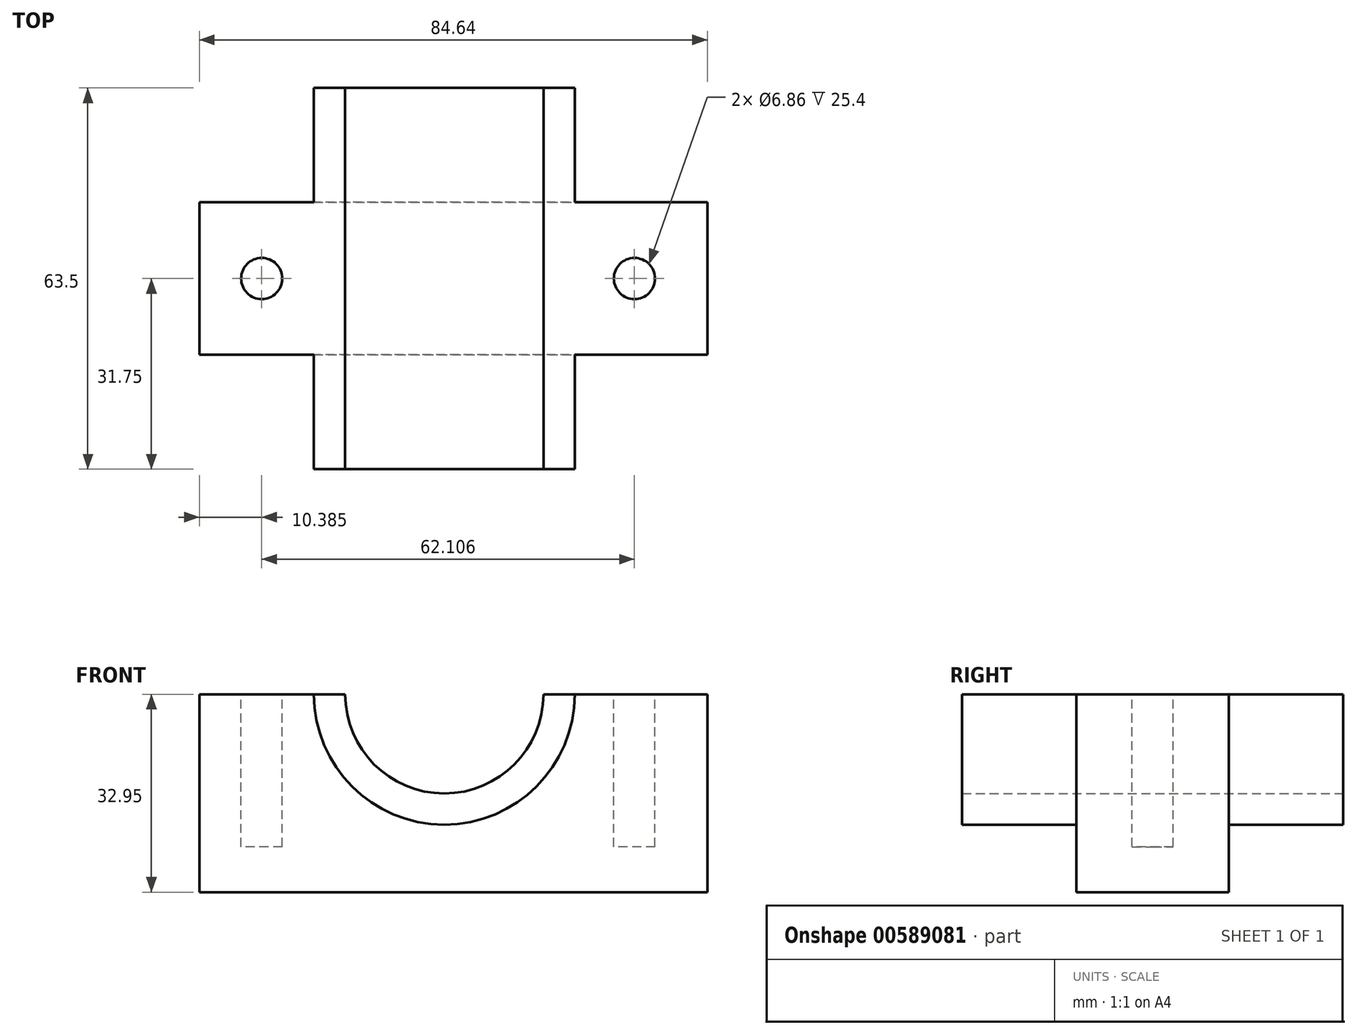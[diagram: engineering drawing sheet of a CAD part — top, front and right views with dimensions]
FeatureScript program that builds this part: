
annotation { "Feature Type Name" : "Feature", "Feature Type Description" : "" }
export const myFeature = defineFeature(function(context is Context, id is Id, definition is map)
    precondition{}
    {
        {
            var Q0;
            Q0=qCreatedBy(makeId("Front.planeOp"),FACE);
            var sketch = newSketch(context, id + "F0", { "sketchPlane" : qUnion([Q0])});
            skLineSegment(sketch, "E0", {"start": v(-40.81, 32.52) * mm, "end": v(43.83, 32.52) * mm});
            skLineSegment(sketch, "E1", {"start": v(43.83, 32.52) * mm, "end": v(43.83, -32.95) * mm});
            skLineSegment(sketch, "E2", {"start": v(43.83, -32.95) * mm, "end": v(-40.81, -32.95) * mm});
            skLineSegment(sketch, "E3", {"start": v(-40.81, -32.95) * mm, "end": v(-40.81, 32.52) * mm});
            skCircle(sketch, "E4", {"center": v(0, 0) * mm, "radius": 16.52 * mm});
            skCircle(sketch, "E5", {"center": v(0, 0) * mm, "radius": 21.72 * mm});
            skSolve(sketch);
        }
        {
            var Q0;
            Q0=makeQuery(id+"F0.imprint","IMPRINT",FACE,{"disambiguationData":[TD([[makeQuery(id+"F0.imprint","IMPRINT",EDGE,{"derivedFrom":sQuery(id+"F0.wireOp",EDGE,"E4")}),-1.0]])]});
            extrude(context, id + "F1", {"entities" : qUnion([Q0]), "endBound" : BoundingType.SYMMETRIC, "depth" : 63.5 * mm, "offsetDistance" : 25.4 * mm});
        }
        {
            var Q0;
            Q0=makeQuery(id+"F0.imprint","IMPRINT",FACE,{"disambiguationData":[TD([[makeQuery(id+"F0.imprint","IMPRINT",EDGE,{"derivedFrom":sQuery(id+"F0.wireOp",EDGE,"E0")}),-1.0]])]});
            extrude(context, id + "F2", {"entities" : qUnion([Q0]), "operationType" : NewBodyOperationType.ADD, "endBound" : BoundingType.SYMMETRIC, "depth" : 25.4 * mm, "offsetDistance" : 25.4 * mm});
        }
        {
            var Q0;
            Q0=qCreatedBy(makeId("Front.planeOp"),FACE);
            var sketch = newSketch(context, id + "F3", { "sketchPlane" : qUnion([Q0])});
            skLineSegment(sketch, "E6", {"start": v(-40.87, 0) * mm, "end": v(43.97, 0) * mm, "construction": true});
            skLineSegment(sketch, "E7.bottom", {"start": v(-40.87, 0) * mm, "end": v(45.51, 0) * mm});
            skLineSegment(sketch, "E7.top", {"start": v(-40.87, 35.08) * mm, "end": v(45.51, 35.08) * mm});
            skLineSegment(sketch, "E7.left", {"start": v(-40.87, 0) * mm, "end": v(-40.87, 35.08) * mm});
            skLineSegment(sketch, "E7.right", {"start": v(45.51, 0) * mm, "end": v(45.51, 35.08) * mm});
            skSolve(sketch);
        }
        {
            var Q0;
            Q0 = qSketchRegion(id + "F3", true);
            extrude(context, id + "F4", {"entities" : qUnion([Q0]), "operationType" : NewBodyOperationType.REMOVE, "endBound" : BoundingType.SYMMETRIC, "oppositeDirection" : true, "depth" : 63.5 * mm, "offsetDistance" : 25.4 * mm});
        }
        {
            var Q0;
            {var subQ2=sQuery(id+"F0.wireOp",EDGE,"E3");Q0=makeQuery(id+"F4.boolean.opBoolean","COPY",FACE,{"disambiguationData":[TD([makeQuery(id+"F2.opExtrude","SWEPT_FACE",FACE,{"disambiguationData":[OSD([subQ2])]})])],"derivedFrom":makeQuery(id+"F4.opExtrude","SWEPT_FACE",FACE,{"disambiguationData":[OSD([sQuery(id+"F3.wireOp",EDGE,"E7.bottom")])]})});}
            var sketch = newSketch(context, id + "F5", { "sketchPlane" : qUnion([Q0])});
            skCircle(sketch, "E8", {"center": v(-30.42, 0) * mm, "radius": 3.43 * mm});
            skCircle(sketch, "E9", {"center": v(31.68, 0) * mm, "radius": 3.43 * mm});
            skSolve(sketch);
        }
        {
            var Q0;
            Q0 = qSketchRegion(id + "F5", true);
            extrude(context, id + "F6", {"entities" : qUnion([Q0]), "operationType" : NewBodyOperationType.REMOVE, "oppositeDirection" : true, "depth" : 25.4 * mm, "offsetDistance" : 25.4 * mm});
        }
    });
